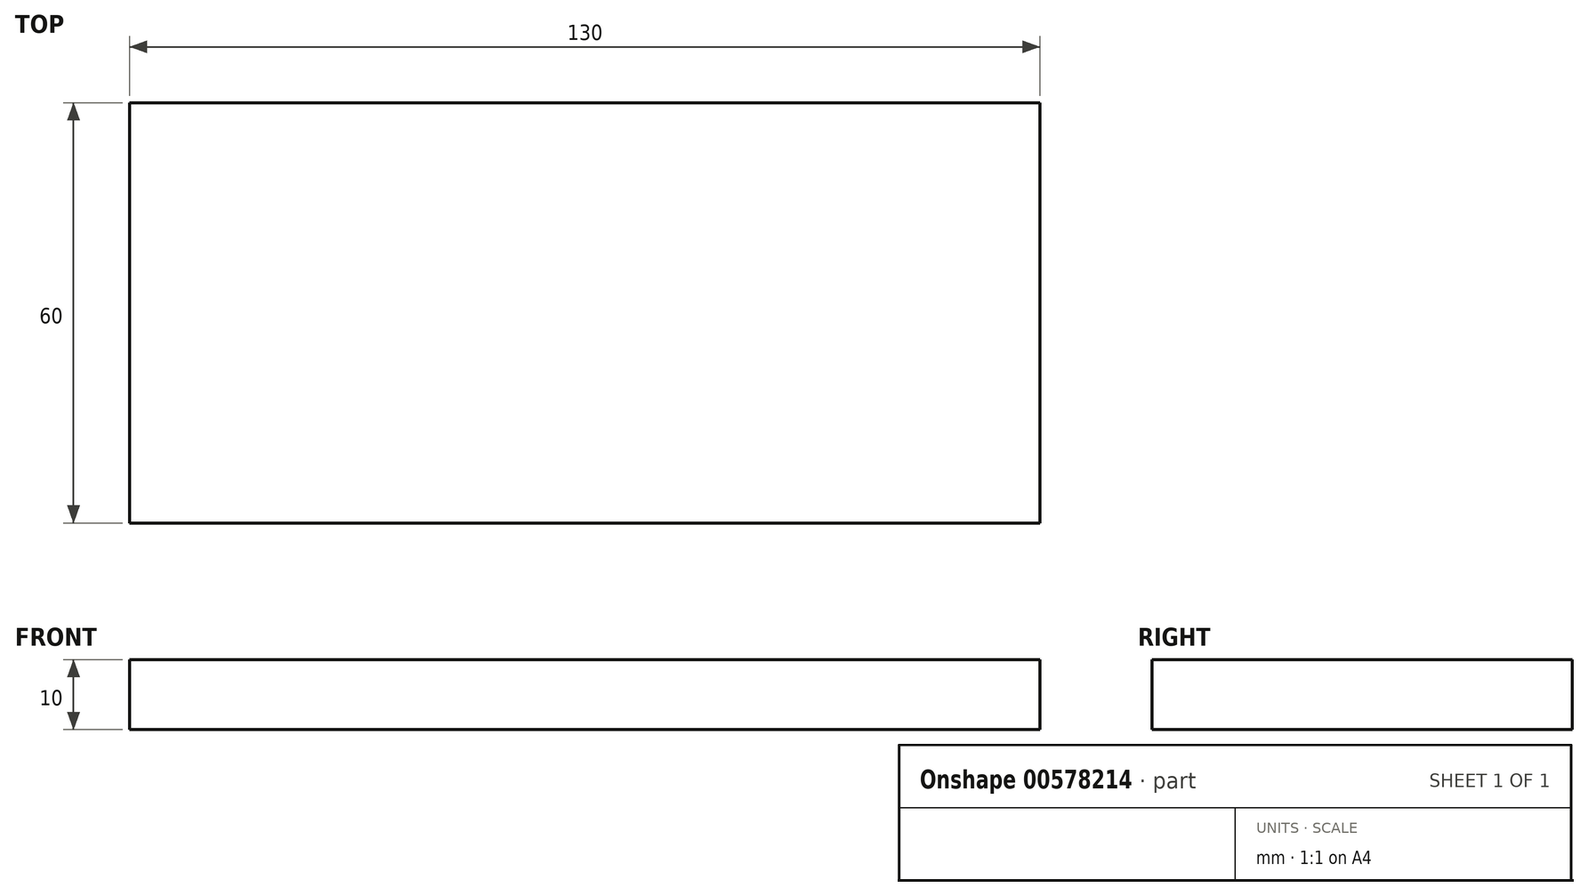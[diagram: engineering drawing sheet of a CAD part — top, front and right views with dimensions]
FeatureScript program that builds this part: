
annotation { "Feature Type Name" : "Feature", "Feature Type Description" : "" }
export const myFeature = defineFeature(function(context is Context, id is Id, definition is map)
    precondition{}
    {
        {
            var Q0;
            Q0=qCreatedBy(makeId("Top.planeOp"),FACE);
            var sketch = newSketch(context, id + "F0", { "sketchPlane" : qUnion([Q0])});
            skLineSegment(sketch, "E0.bottom", {"start": v(65, -30) * mm, "end": v(-65, -30) * mm});
            skLineSegment(sketch, "E0.top", {"start": v(65, 30) * mm, "end": v(-65, 30) * mm});
            skLineSegment(sketch, "E0.left", {"start": v(65, -30) * mm, "end": v(65, 30) * mm});
            skLineSegment(sketch, "E0.right", {"start": v(-65, -30) * mm, "end": v(-65, 30) * mm});
            skPoint(sketch, "E0.middle", {"position": v(0, 0) * mm});
            skSolve(sketch);
        }
        {
            var Q0;
            Q0=qSketchRegion(id+"F0",true);
            extrude(context, id + "F1", {"entities" : qUnion([Q0]), "endBound" : BoundingType.SYMMETRIC, "depth" : 10 * mm, "offsetDistance" : 25 * mm});
        }
    });
